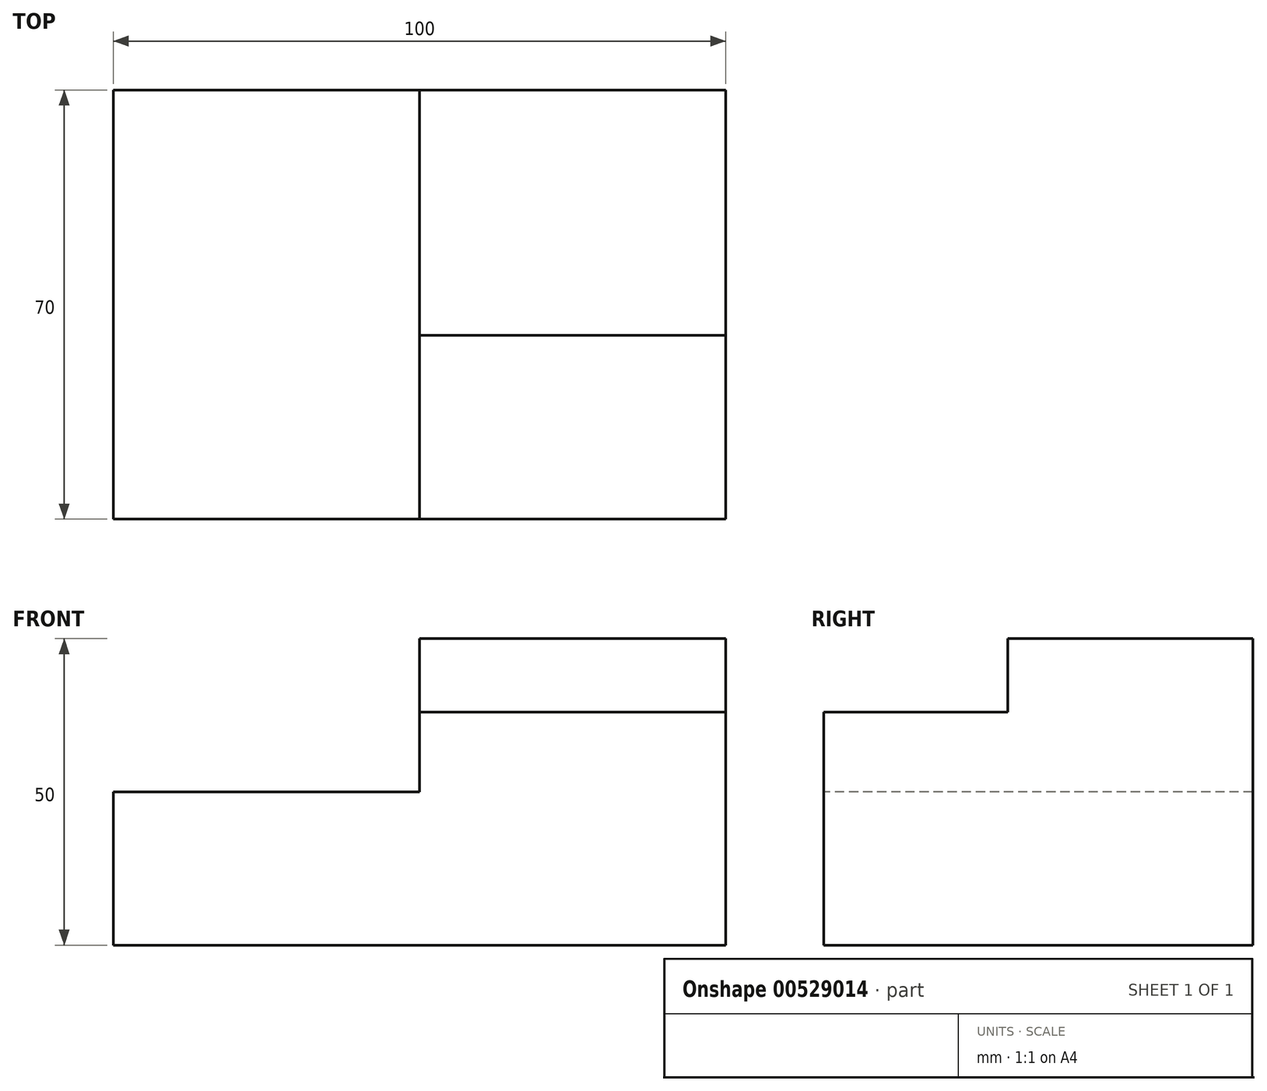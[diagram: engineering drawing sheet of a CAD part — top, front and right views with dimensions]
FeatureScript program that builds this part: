
annotation { "Feature Type Name" : "Feature", "Feature Type Description" : "" }
export const myFeature = defineFeature(function(context is Context, id is Id, definition is map)
    precondition{}
    {
        {
            var Q0;
            Q0=qCreatedBy(makeId("Front.planeOp"),FACE);
            var sketch = newSketch(context, id + "F0", { "sketchPlane" : qUnion([Q0])});
            skLineSegment(sketch, "E0", {"start": v(-50, -32.84) * mm, "end": v(50, -32.84) * mm});
            skLineSegment(sketch, "E1", {"start": v(50, -32.84) * mm, "end": v(50, 5.16) * mm});
            skLineSegment(sketch, "E2", {"start": v(50, 5.16) * mm, "end": v(0, 5.16) * mm});
            skLineSegment(sketch, "E3", {"start": v(0, 5.16) * mm, "end": v(0, -7.84) * mm});
            skLineSegment(sketch, "E4", {"start": v(0, -7.84) * mm, "end": v(-50, -7.84) * mm});
            skLineSegment(sketch, "E5", {"start": v(-50, -32.84) * mm, "end": v(-50, -7.84) * mm});
            skLineSegment(sketch, "E6", {"start": v(50, 5.16) * mm, "end": v(50, 17.16) * mm});
            skLineSegment(sketch, "E7", {"start": v(50, 17.16) * mm, "end": v(0, 17.16) * mm});
            skLineSegment(sketch, "E8", {"start": v(0, 17.16) * mm, "end": v(0, 5.16) * mm});
            skLineSegment(sketch, "E9", {"start": v(0, 5.16) * mm, "end": v(5.15, 5.16) * mm});
            skSolve(sketch);
        }
        {
            var Q0;
            Q0 = qSketchRegion(id + "F0", true);
            extrude(context, id + "F1", {"entities" : qUnion([Q0]), "oppositeDirection" : true, "depth" : 70 * mm, "offsetDistance" : 25 * mm});
        }
        {
            var Q0;
            Q0=makeQuery(id+"F1.opExtrude","SWEPT_FACE",FACE,{"disambiguationData":[OSD([sQuery(id+"F0.wireOp",EDGE,"E7")])]});
            var sketch = newSketch(context, id + "F2", { "sketchPlane" : qUnion([Q0])});
            skLineSegment(sketch, "E10", {"start": v(0, 0) * mm, "end": v(0, 30) * mm});
            skLineSegment(sketch, "E11", {"start": v(0, 30) * mm, "end": v(50, 30) * mm});
            skSolve(sketch);
        }
        {
            var Q0;
            Q0 = qSketchRegion(id + "F2", true);
            var Q1;
            Q1=makeQuery(id+"F2.imprint","IMPRINT",FACE,{"disambiguationData":[TD([[makeQuery(id+"F2.imprint","IMPRINT",EDGE,{"derivedFrom":sQuery(id+"F2.wireOp",EDGE,"E10")}),1.0]])]});
            extrude(context, id + "F3", {"entities" : qUnion([Q0, Q1]), "operationType" : NewBodyOperationType.REMOVE, "oppositeDirection" : true, "depth" : 12 * mm, "offsetDistance" : 25 * mm});
        }
    });
